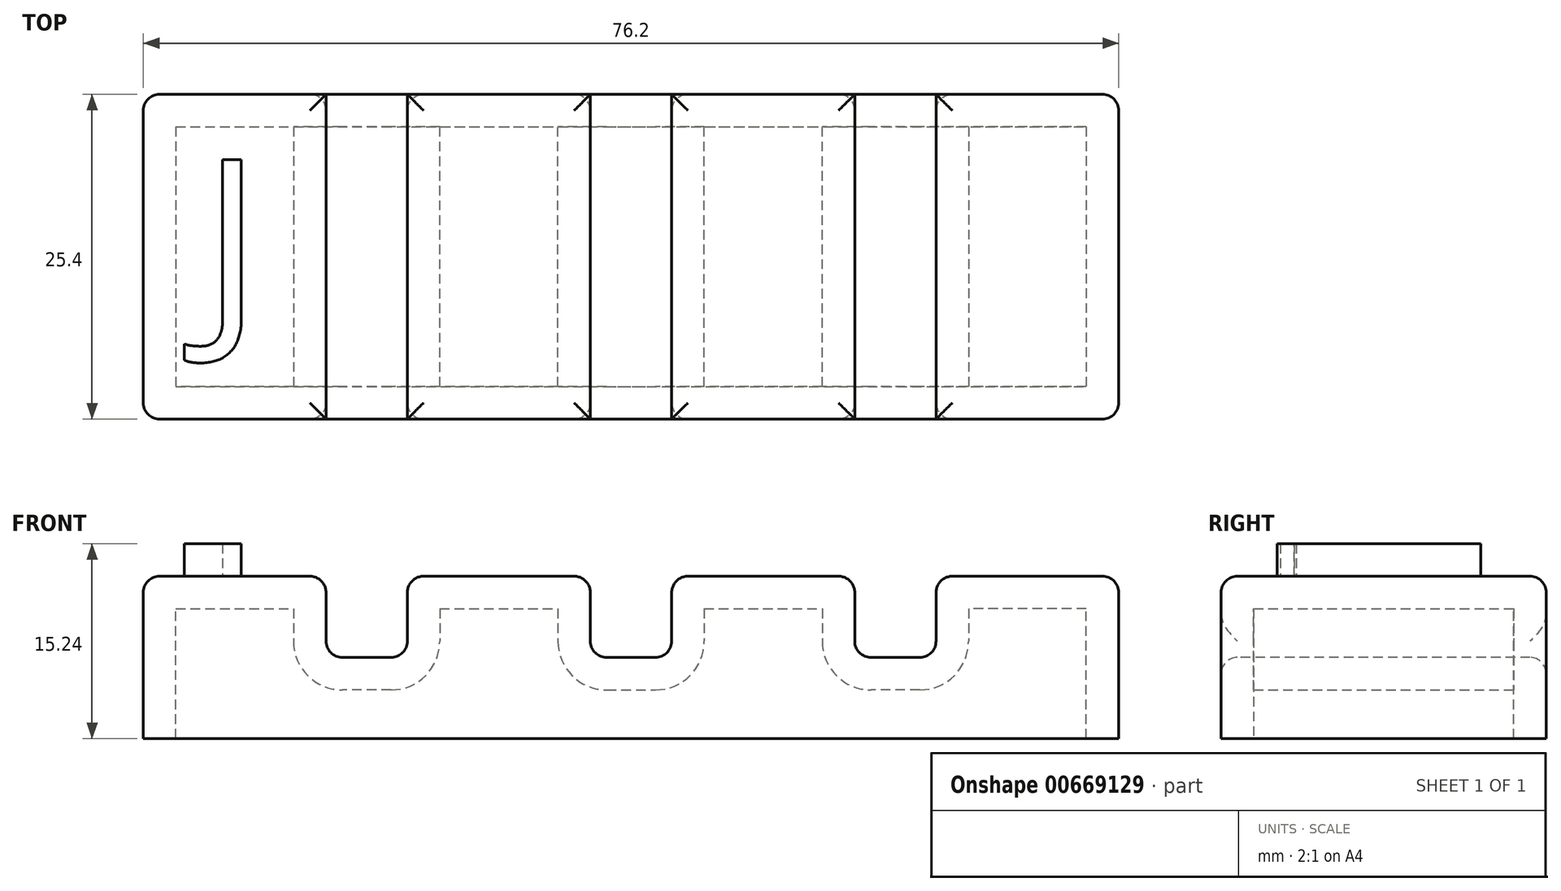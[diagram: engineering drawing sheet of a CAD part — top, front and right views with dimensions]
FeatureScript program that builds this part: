
annotation { "Feature Type Name" : "Feature", "Feature Type Description" : "" }
export const myFeature = defineFeature(function(context is Context, id is Id, definition is map)
    precondition{}
    {
        {
            var Q0;
            Q0=qCreatedBy(makeId("Top.planeOp"),FACE);
            var sketch = newSketch(context, id + "F0", { "sketchPlane" : qUnion([Q0])});
            skLineSegment(sketch, "E0.bottom", {"start": v(-38.1, 12.7) * mm, "end": v(38.1, 12.7) * mm});
            skLineSegment(sketch, "E0.top", {"start": v(-38.1, -12.7) * mm, "end": v(38.1, -12.7) * mm});
            skLineSegment(sketch, "E0.left", {"start": v(-38.1, 12.7) * mm, "end": v(-38.1, -12.7) * mm});
            skLineSegment(sketch, "E0.right", {"start": v(38.1, 12.7) * mm, "end": v(38.1, -12.7) * mm});
            skPoint(sketch, "E0.middle", {"position": v(0, 0) * mm});
            skSolve(sketch);
        }
        {
            var Q0;
            Q0 = qSketchRegion(id + "F0", true);
            extrude(context, id + "F1", {"entities" : qUnion([Q0]), "depth" : 12.7 * mm, "offsetDistance" : 25.4 * mm});
        }
        {
            var Q0;
            Q0=makeQuery(id+"F1.opExtrude","SWEPT_FACE",FACE,{"disambiguationData":[OSD([sQuery(id+"F0.wireOp",EDGE,"E0.top")])]});
            var sketch = newSketch(context, id + "F2", { "sketchPlane" : qUnion([Q0])});
            skLineSegment(sketch, "E1", {"start": v(-38.1, 6.35) * mm, "end": v(38.1, 6.35) * mm, "construction": true});
            skPoint(sketch, "E2.middle", {"position": v(0, 12.7) * mm});
            skLineSegment(sketch, "E3.bottom", {"start": v(17.48, 6.35) * mm, "end": v(23.83, 6.35) * mm});
            skLineSegment(sketch, "E3.top", {"start": v(17.48, 19.05) * mm, "end": v(23.83, 19.05) * mm});
            skLineSegment(sketch, "E3.left", {"start": v(17.48, 6.35) * mm, "end": v(17.48, 19.05) * mm});
            skLineSegment(sketch, "E3.right", {"start": v(23.83, 6.35) * mm, "end": v(23.83, 19.05) * mm});
            skPoint(sketch, "E3.middle", {"position": v(20.65, 12.7) * mm});
            skLineSegment(sketch, "E4.bottom", {"start": v(-23.83, 6.35) * mm, "end": v(-17.48, 6.35) * mm});
            skLineSegment(sketch, "E4.top", {"start": v(-23.83, 19.05) * mm, "end": v(-17.48, 19.05) * mm});
            skLineSegment(sketch, "E4.left", {"start": v(-23.83, 6.35) * mm, "end": v(-23.83, 19.05) * mm});
            skLineSegment(sketch, "E4.right", {"start": v(-17.48, 6.35) * mm, "end": v(-17.48, 19.05) * mm});
            skPoint(sketch, "E4.middle", {"position": v(-20.65, 12.7) * mm});
            skLineSegment(sketch, "E5.bottom", {"start": v(3.17, 6.35) * mm, "end": v(-3.18, 6.35) * mm});
            skLineSegment(sketch, "E5.top", {"start": v(3.17, 19.05) * mm, "end": v(-3.18, 19.05) * mm});
            skLineSegment(sketch, "E5.left", {"start": v(3.17, 6.35) * mm, "end": v(3.17, 19.05) * mm});
            skLineSegment(sketch, "E5.right", {"start": v(-3.18, 6.35) * mm, "end": v(-3.18, 19.05) * mm});
            skSolve(sketch);
        }
        {
            var Q0;
            Q0 = qSketchRegion(id + "F2", true);
            extrude(context, id + "F3", {"entities" : qUnion([Q0]), "operationType" : NewBodyOperationType.REMOVE, "endBound" : BoundingType.THROUGH_ALL, "oppositeDirection" : true, "depth" : 25.4 * mm, "offsetDistance" : 25.4 * mm});
        }
        {
            var Q0;
            {var subQ0=sQuery(id+"F0.wireOp",EDGE,"E0.bottom");var subQ1=sQuery(id+"F0.wireOp",EDGE,"E0.top");var subQ2=sQuery(id+"F0.wireOp",EDGE,"E0.left");Q0=makeQuery(id+"F3.boolean.opBoolean","SPLIT",FACE,{"disambiguationData":[TD([makeQuery(id+"F1.opExtrude","SWEPT_FACE",FACE,{"disambiguationData":[OSD([subQ2])]})])],"derivedFrom":makeQuery(id+"F1.opExtrude","CAP_FACE",FACE,{"disambiguationData":[OSD([subQ0,subQ1,subQ2,sQuery(id+"F0.wireOp",EDGE,"E0.right")])],"isStart":false})});}
            var Q1;
            {var subQ0=sQuery(id+"F0.wireOp",EDGE,"E0.bottom");var subQ1=sQuery(id+"F0.wireOp",EDGE,"E0.top");Q1=makeQuery(id+"F3.boolean.opBoolean","SPLIT",FACE,{"disambiguationData":[TD([makeQuery(id+"F3.opExtrude","SWEPT_FACE",FACE,{"disambiguationData":[OSD([sQuery(id+"F2.wireOp",EDGE,"E4.right")])]})])],"derivedFrom":makeQuery(id+"F1.opExtrude","CAP_FACE",FACE,{"disambiguationData":[OSD([subQ0,subQ1,sQuery(id+"F0.wireOp",EDGE,"E0.left"),sQuery(id+"F0.wireOp",EDGE,"E0.right")])],"isStart":false})});}
            var Q2;
            {var subQ0=sQuery(id+"F0.wireOp",EDGE,"E0.bottom");var subQ1=sQuery(id+"F0.wireOp",EDGE,"E0.top");Q2=makeQuery(id+"F3.boolean.opBoolean","SPLIT",FACE,{"disambiguationData":[TD([makeQuery(id+"F3.opExtrude","SWEPT_FACE",FACE,{"disambiguationData":[OSD([sQuery(id+"F2.wireOp",EDGE,"E3.left")])]})])],"derivedFrom":makeQuery(id+"F1.opExtrude","CAP_FACE",FACE,{"disambiguationData":[OSD([subQ0,subQ1,sQuery(id+"F0.wireOp",EDGE,"E0.left"),sQuery(id+"F0.wireOp",EDGE,"E0.right")])],"isStart":false})});}
            var Q3;
            {var subQ0=sQuery(id+"F0.wireOp",EDGE,"E0.bottom");var subQ1=sQuery(id+"F0.wireOp",EDGE,"E0.right");var subQ2=sQuery(id+"F0.wireOp",EDGE,"E0.top");Q3=makeQuery(id+"F3.boolean.opBoolean","SPLIT",FACE,{"disambiguationData":[TD([makeQuery(id+"F1.opExtrude","SWEPT_FACE",FACE,{"disambiguationData":[OSD([subQ1])]})])],"derivedFrom":makeQuery(id+"F1.opExtrude","CAP_FACE",FACE,{"disambiguationData":[OSD([subQ0,subQ2,sQuery(id+"F0.wireOp",EDGE,"E0.left"),subQ1])],"isStart":false})});}
            var Q4;
            Q4=makeQuery(id+"F3.boolean.opBoolean","COPY",FACE,{"derivedFrom":makeQuery(id+"F3.opExtrude","SWEPT_FACE",FACE,{"disambiguationData":[OSD([sQuery(id+"F2.wireOp",EDGE,"E4.bottom")])]})});
            var Q5;
            Q5=makeQuery(id+"F3.boolean.opBoolean","COPY",FACE,{"derivedFrom":makeQuery(id+"F3.opExtrude","SWEPT_FACE",FACE,{"disambiguationData":[OSD([sQuery(id+"F2.wireOp",EDGE,"E5.bottom")])]})});
            var Q6;
            Q6=makeQuery(id+"F3.boolean.opBoolean","COPY",FACE,{"derivedFrom":makeQuery(id+"F3.opExtrude","SWEPT_FACE",FACE,{"disambiguationData":[OSD([sQuery(id+"F2.wireOp",EDGE,"E3.bottom")])]})});
            var Q7;
            Q7=makeQuery(id+"F1.opExtrude","SWEPT_EDGE",EDGE,{"disambiguationData":[OSD([sQuery(id+"F0.wireOp",EDGE,"E0.top"),sQuery(id+"F0.wireOp",EDGE,"E0.right")])]});
            var Q8;
            Q8=makeQuery(id+"F1.opExtrude","SWEPT_EDGE",EDGE,{"disambiguationData":[OSD([sQuery(id+"F0.wireOp",EDGE,"E0.bottom"),sQuery(id+"F0.wireOp",EDGE,"E0.right")])]});
            var Q9;
            Q9=makeQuery(id+"F1.opExtrude","SWEPT_EDGE",EDGE,{"disambiguationData":[OSD([sQuery(id+"F0.wireOp",EDGE,"E0.top"),sQuery(id+"F0.wireOp",EDGE,"E0.left")])]});
            var Q10;
            Q10=makeQuery(id+"F1.opExtrude","SWEPT_EDGE",EDGE,{"disambiguationData":[OSD([sQuery(id+"F0.wireOp",EDGE,"E0.bottom"),sQuery(id+"F0.wireOp",EDGE,"E0.left")])]});
            fillet(context, id + "F4", {"entities" : qUnion([Q0, Q1, Q2, Q3, Q4, Q5, Q6, Q7, Q8, Q9, Q10]), "radius" : 1.27 * mm, "tangentPropagation" : true, "allowEdgeOverflow" : false});
        }
        {
            var Q0;
            Q0=makeQuery(id+"F1.opExtrude","CAP_FACE",FACE,{"disambiguationData":[OSD([sQuery(id+"F0.wireOp",EDGE,"E0.bottom"),sQuery(id+"F0.wireOp",EDGE,"E0.top"),sQuery(id+"F0.wireOp",EDGE,"E0.left"),sQuery(id+"F0.wireOp",EDGE,"E0.right")])],"isStart":true});
            shell(context, id + "F5", {"entities" : qUnion([Q0]), "thickness" : 2.54 * mm});
        }
        {
            var Q0;
            {var subQ0=sQuery(id+"F0.wireOp",EDGE,"E0.bottom");var subQ1=sQuery(id+"F0.wireOp",EDGE,"E0.top");var subQ2=sQuery(id+"F0.wireOp",EDGE,"E0.left");Q0=makeQuery(id+"F3.boolean.opBoolean","SPLIT",FACE,{"disambiguationData":[TD([makeQuery(id+"F1.opExtrude","SWEPT_FACE",FACE,{"disambiguationData":[OSD([subQ2])]})])],"derivedFrom":makeQuery(id+"F1.opExtrude","CAP_FACE",FACE,{"disambiguationData":[OSD([subQ0,subQ1,subQ2,sQuery(id+"F0.wireOp",EDGE,"E0.right")])],"isStart":false})});}
            var sketch = newSketch(context, id + "F6", { "sketchPlane" : qUnion([Q0])});
            skText(sketch, "E6", { "text": "J", "fontName": "OpenSans-Regular.ttf"});
            const initialGuessF6  = {"E6": [-0.03354, -0.005, 1, 0, 0.01269]};
            skSetInitialGuess(sketch, initialGuessF6);
            skSolve(sketch);
        }
        {
            var Q0;
            Q0 = qSketchRegion(id + "F6", true);
            extrude(context, id + "F7", {"entities" : qUnion([Q0]), "operationType" : NewBodyOperationType.ADD, "depth" : 2.54 * mm, "offsetDistance" : 25.4 * mm});
        }
    });
